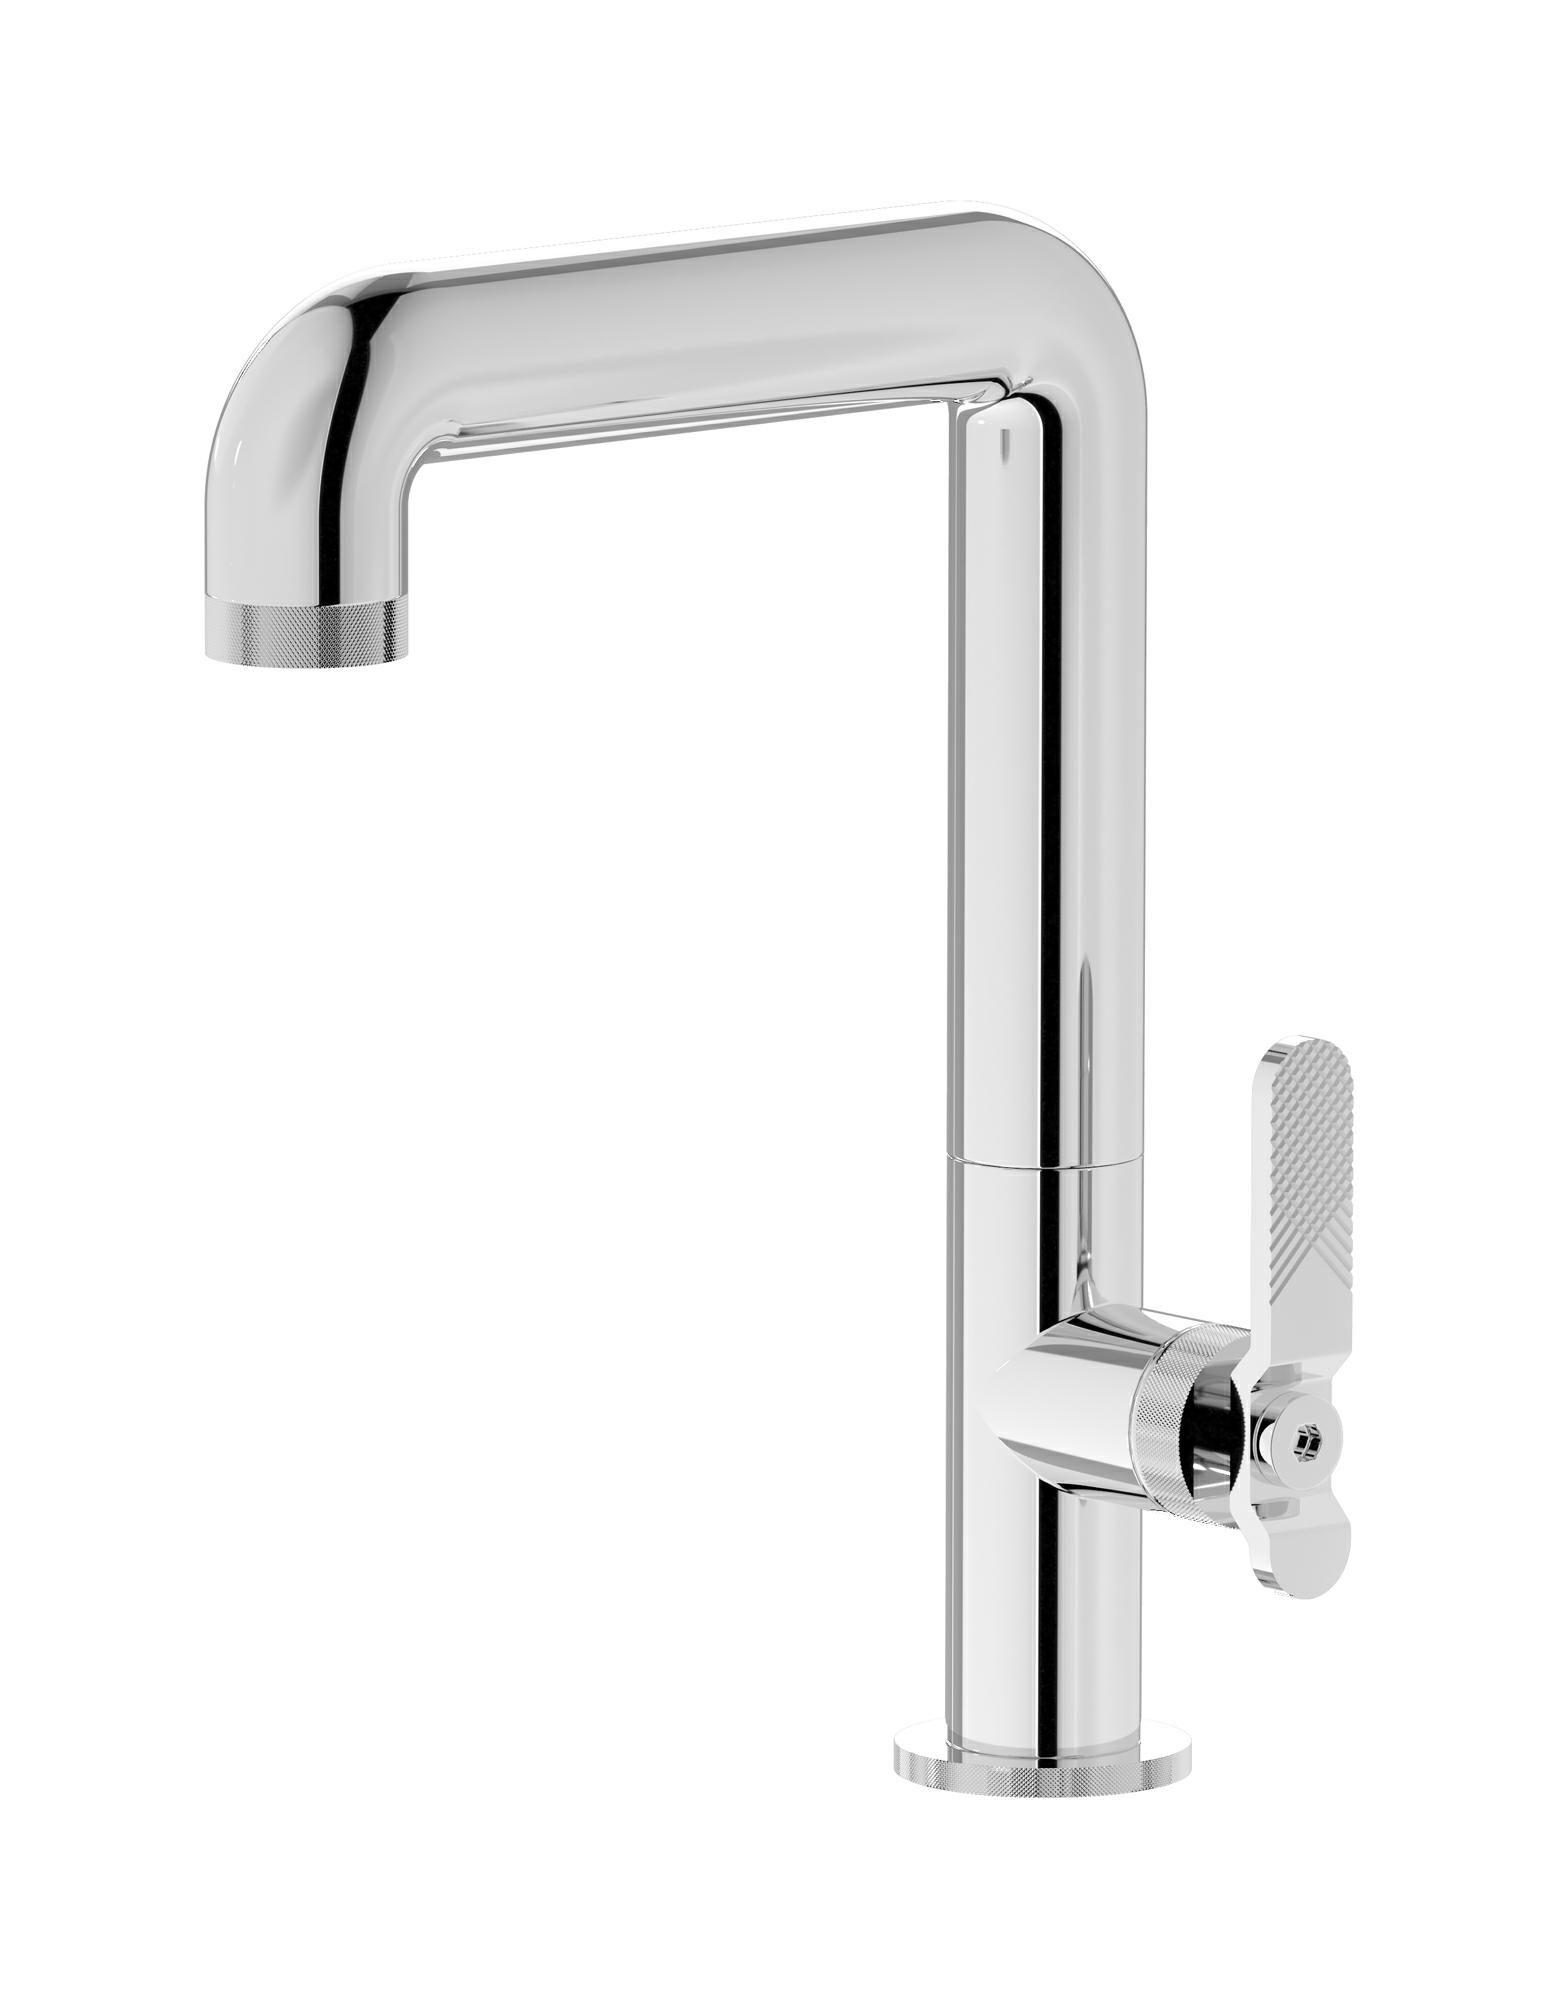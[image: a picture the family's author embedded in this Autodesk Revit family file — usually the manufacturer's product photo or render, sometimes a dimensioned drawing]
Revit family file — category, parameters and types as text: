
# Revit family: B2202
name_source: partatom
category: Apparecchi idraulici
units: mm (PartAtom-declared; Revit-internal decimal feet)

## family parameters
Basato su piano di lavoro = No
Condiviso = No
Mantieni orientamento annotazione = No
Numero OmniClass = 23.45.55.17
Punto di calcolo locali = No
Quota connettore circolare = Usa diametro
Sempre verticale = Sì
Taglio con vuoti quando caricato = No
Tipo di parte = Normale
Titolo OmniClass = Mixing Faucets

## types (13) — shared parameters
Cold water inlet = 10 mm  [stored 0.0328084 ft]
Commenti sul tipo = Tall monohole washbasin mixer complete with drain
Connessione CW = No
Connessione HW = No
Connessione di scarico = No
Connessione di ventilazione = No
Descrizione = Tall monohole washbasin mixer complete with drain
Hot water inlet = 10 mm  [stored 0.0328084 ft]
Produttore = IB Rubinetterie S.p.A.
URL = https://www.weareib.it
zero-valued in all types: Prospetto di default

## per-type parameters (varying)
| type | Finishes surface | Immagine tipo | Modello |
| Chrome | IB_Chrome | B2202CC.jpg | B2202CC |
| Black Chrome | IB_Black chrome | B2202CF.jpg | B2202CF |
| Brushed Black Chrome | IB_Brushed black chrome | B2202CS.jpg | B2202CS |
| Brushed Pale Gold | IB_brushed pale gold | B2202IS.jpg | B2202IS |
| Pale Gold | IB_Pale gold | B2202II.jpg | B2202II |
| Matt Black | IB_matt black | B2202NP.jpg | B2202NP |
| Natural Brass | IB_Brass | B2202ON.jpg | B2202ON |
| Gold | IB_gold | B2202OO.jpg | B2202OO |
| Brushed Gold | IB_brushed gold | B2202OS.jpg | B2202OS |
| Rose Gold | IB_Rose gold | B2202RS.jpg | B2202RS |
| Brushed Rose Gold | IB_Brushed rose gold | B2202SR.jpg | B2202SR |
| Brushed Nickel | IB_Brushed nickel | B2202SS.jpg | B2202SS |
| Modern Bronze | IB_Modern bronze | B2202MB.jpg | B2202MB |

note: [stored X ft] marks values corroborated as IEEE doubles in the binary element streams (Revit-internal decimal feet)
